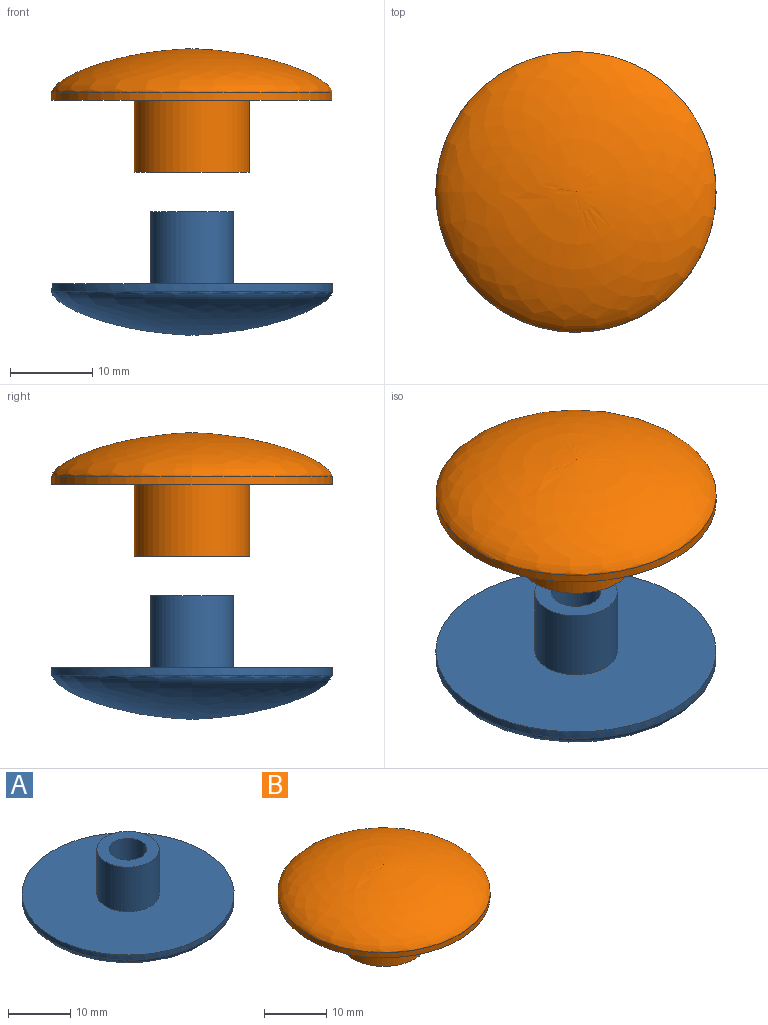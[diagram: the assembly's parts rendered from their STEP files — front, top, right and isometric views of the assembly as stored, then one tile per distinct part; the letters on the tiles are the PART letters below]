
ASSEMBLY  parts=2 mates=1
PART A: 7 faces, bbox 34x34x15 mm
  f0: cylinder r=17mm len=34mm, axis (0,0,1), area 106.8mm2, adj f1,f6
  f1: revolved ~34x34mm, area 1029.8mm2, adj f0
  f2: plane 6x6mm, normal (0,0,1), area 28.3mm2, adj f3
  f3: cylinder r=3mm len=8.75mm, axis (0,0,1), area 164.9mm2, adj f2,f4
  f4: plane 10x10mm, normal (0,0,1), area 50.3mm2, adj f3,f5
  f5: cylinder r=5mm len=10mm, axis (0,0,1), area 274.8mm2, adj f4,f6
  f6: plane 34x34mm, normal (0,0,1), area 829.4mm2, adj f0,f5
PART B: 7 faces, bbox 34x34x15 mm
  f0: plane 10x10mm, normal (0,0,-1), area 78.5mm2, adj f6
  f1: revolved ~34x34mm, area 1029.8mm2, adj f2
  f2: cylinder r=17mm len=34mm, axis (0,0,-1), area 106.8mm2, adj f1,f3
  f3: plane 34x34mm, normal (0,0,-1), area 754mm2, adj f2,f4
  f4: cylinder r=7mm len=14mm, axis (0,0,-1), area 384.7mm2, adj f3,f5
  f5: plane 14x14mm, normal (0,0,-1), area 75.4mm2, adj f4,f6
  f6: cylinder r=5mm len=10mm, axis (0,0,-1), area 274.8mm2, adj f0,f5
PLACE A t=(-11.54,25.03,31.95)mm
PLACE B t=(-11.45,25.03,27.84)mm
MATE slider A.f0 <-> B.f2  axis (0,0,1) through (-11.45,25.03,14.29)mm
